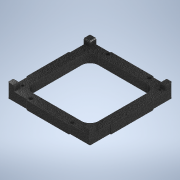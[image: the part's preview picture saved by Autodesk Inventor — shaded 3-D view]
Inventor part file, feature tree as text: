
AUTODESK INVENTOR PART (.ipt)
format: ipt  version: 2022 (Build 260153000, 153)  size: 315,904 bytes
history: native  units: mm
features: extrude x6, sketch x6, projected_geometry x4, fillet x2, chamfer x1
ambient origin geometry x8: Origin, YZ Plane, XZ Plane, XY Plane, X Axis, Y Axis, Z Axis, Center Point
bodies: Solid1 (feature_tree)
feature tree (19):
  extrude  "Extrusion1"  Depth=73.66mm
  extrude  "Extrusion2"  Depth=2.54mm
  extrude  "Extrusion3"  Depth=100.0mm
  fillet  "Fillet1"  Radius=100.0mm
  extrude  "Extrusion4"  Depth=10.0mm TaperAngle=0.0deg
  chamfer  "Chamfer1"  Distance=4.5mm
  extrude  "Extrusion5"  Depth=6.5mm
  fillet  "Fillet2"  Radius=6.2mm
  extrude  "Extrusion6"  Depth=1.2mm
  sketch  "Sketch1"  dims[d0=73.66mm d1=80.01mm]
  sketch  "Sketch4"  dims[d2=85.730001mm d3=2.54mm]
  projected_geometry  "Projected Loop2"
  sketch  "Sketch5"  dims[d4=3.81mm d6=2.9mm d7=100.0mm]
  projected_geometry  "Projected Loop3"
  sketch  "Sketch6"  dims[d8=100.0mm d10=10.0mm d11=0.0mm]
  projected_geometry  "Projected Loop4"
  sketch  "Sketch7"  dims[d13=4.5mm]
  projected_geometry  "Projected Loop5"
  sketch  "Sketch8"  dims[d14=4.5mm d15=4.5mm d16=4.5mm d17=6.2mm d18=0.0mm d19=1.2mm d20=1.2mm d21=25.0mm d22=25.0mm d23=0.0mm d24=0.0mm d25=40.0mm d27=360.0deg d29=1.0mm d30=7.3mm d31=7.3mm d32=6.5mm d33=0.0mm d34=1.0mm d35=2.0mm d36=45.0deg d37=40.0mm d39=360.0deg d50=11.0mm d51=11.0mm d52=11.0mm d53=11.0mm d54=10.0mm d55=0.0mm d56=10.0mm d57=49.4mm d58=91.6mm d59=4.2mm d60=4.2mm d61=4.2mm d62=4.2mm d63=6.5mm d64=0.0mm]
